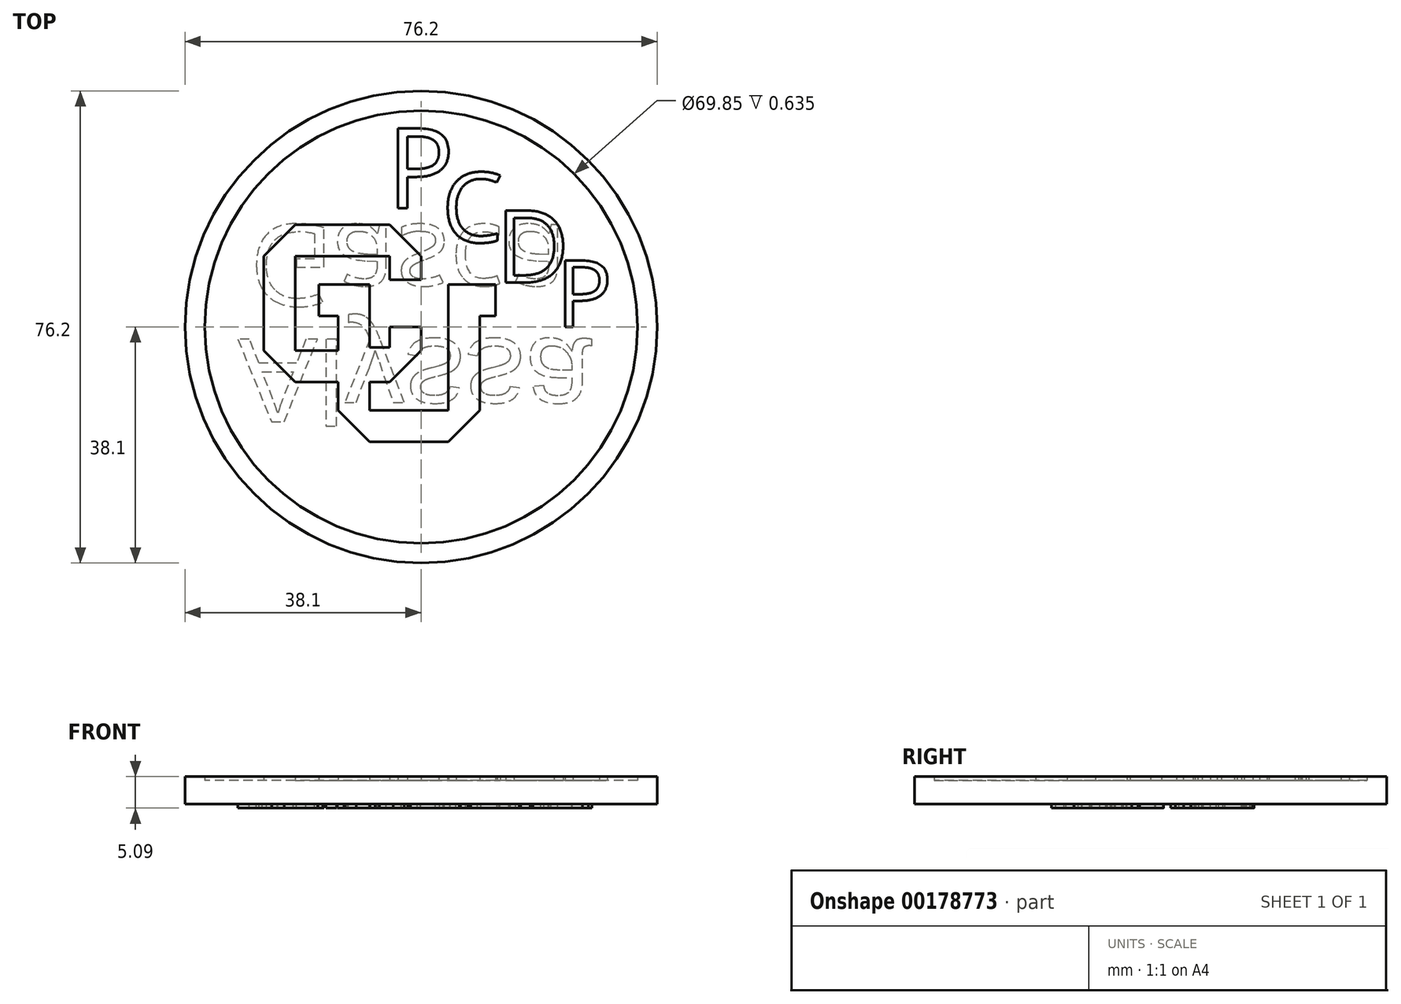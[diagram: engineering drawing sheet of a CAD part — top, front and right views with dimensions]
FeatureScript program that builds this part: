
annotation { "Feature Type Name" : "Feature", "Feature Type Description" : "" }
export const myFeature = defineFeature(function(context is Context, id is Id, definition is map)
    precondition{}
    {
        {
            var Q0;
            Q0=qCreatedBy(makeId("Top.planeOp"),FACE);
            var sketch = newSketch(context, id + "F0", { "sketchPlane" : qUnion([Q0])});
            skCircle(sketch, "E0", {"center": v(0, 0) * mm, "radius": 38.1 * mm});
            skSolve(sketch);
        }
        {
            var Q0;
            Q0=makeQuery(id+"F0.imprint","IMPRINT",FACE,{"disambiguationData":[TD([[makeQuery(id+"F0.imprint","IMPRINT",EDGE,{"derivedFrom":sQuery(id+"F0.wireOp",EDGE,"E0")}),1.0]])]});
            extrude(context, id + "F1", {"entities" : qUnion([Q0]), "depth" : 3.8 * mm});
        }
        {
            var Q0;
            Q0=makeQuery(id+"F1.opExtrude","CAP_FACE",FACE,{"disambiguationData":[OSD([sQuery(id+"F0.wireOp",EDGE,"E0")])],"isStart":false});
            var sketch = newSketch(context, id + "F2", { "sketchPlane" : qUnion([Q0])});
            skCircle(sketch, "E1", {"center": v(0, 0) * mm, "radius": 38.1 * mm});
            skCircle(sketch, "E2", {"center": v(0, 0) * mm, "radius": 34.93 * mm});
            skLineSegment(sketch, "E3", {"start": v(0, 0) * mm, "end": v(0, -3.81) * mm});
            skLineSegment(sketch, "E4", {"start": v(0, -3.81) * mm, "end": v(-5.08, -8.9) * mm});
            skLineSegment(sketch, "E5", {"start": v(-20.32, -8.9) * mm, "end": v(-25.4, -3.81) * mm});
            skLineSegment(sketch, "E6", {"start": v(-25.4, -3.81) * mm, "end": v(-25.4, 11.43) * mm});
            skLineSegment(sketch, "E7", {"start": v(-25.4, 11.43) * mm, "end": v(-20.32, 16.5) * mm});
            skLineSegment(sketch, "E8", {"start": v(-20.32, 16.5) * mm, "end": v(-5.08, 16.5) * mm});
            skLineSegment(sketch, "E9", {"start": v(-5.08, 16.5) * mm, "end": v(0, 11.43) * mm});
            skLineSegment(sketch, "E10", {"start": v(0, 11.43) * mm, "end": v(0, 7.62) * mm});
            skLineSegment(sketch, "E11", {"start": v(0, 7.62) * mm, "end": v(-5.08, 7.62) * mm});
            skLineSegment(sketch, "E12", {"start": v(-5.08, 7.62) * mm, "end": v(-5.08, 11.43) * mm});
            skLineSegment(sketch, "E13", {"start": v(-5.08, 11.43) * mm, "end": v(-20.32, 11.43) * mm});
            skLineSegment(sketch, "E14", {"start": v(-20.32, 11.43) * mm, "end": v(-20.32, -3.81) * mm});
            skLineSegment(sketch, "E15", {"start": v(-5.08, -3.28) * mm, "end": v(-5.08, 0) * mm});
            skLineSegment(sketch, "E16", {"start": v(-5.08, 0) * mm, "end": v(0, 0) * mm});
            skLineSegment(sketch, "E17", {"start": v(-16.51, 6.88) * mm, "end": v(-16.51, 1.8) * mm});
            skLineSegment(sketch, "E18", {"start": v(-16.51, 1.8) * mm, "end": v(-13.36, 1.8) * mm});
            skLineSegment(sketch, "E19", {"start": v(-16.51, 6.88) * mm, "end": v(-8.28, 6.88) * mm});
            skLineSegment(sketch, "E20", {"start": v(-13.36, -13.44) * mm, "end": v(-8.28, -18.52) * mm});
            skLineSegment(sketch, "E21", {"start": v(-8.28, -18.52) * mm, "end": v(4.42, -18.52) * mm});
            skLineSegment(sketch, "E22", {"start": v(4.42, -18.52) * mm, "end": v(9.5, -13.44) * mm});
            skLineSegment(sketch, "E23", {"start": v(9.5, -13.44) * mm, "end": v(9.5, 1.8) * mm});
            skLineSegment(sketch, "E24", {"start": v(9.5, 1.8) * mm, "end": v(12.04, 1.8) * mm});
            skLineSegment(sketch, "E25", {"start": v(12.04, 1.8) * mm, "end": v(12.04, 6.88) * mm});
            skLineSegment(sketch, "E26", {"start": v(12.04, 6.88) * mm, "end": v(4.42, 6.88) * mm});
            skLineSegment(sketch, "E27", {"start": v(4.42, 6.88) * mm, "end": v(4.42, -13.44) * mm});
            skLineSegment(sketch, "E28", {"start": v(-13.36, 1.8) * mm, "end": v(-13.36, -3.81) * mm});
            skLineSegment(sketch, "E29", {"start": v(-20.32, -3.81) * mm, "end": v(-13.36, -3.81) * mm});
            skLineSegment(sketch, "E30", {"start": v(-20.32, -8.9) * mm, "end": v(-13.36, -8.9) * mm});
            skLineSegment(sketch, "E31", {"start": v(-13.36, -8.9) * mm, "end": v(-13.36, -13.44) * mm});
            skLineSegment(sketch, "E32", {"start": v(-8.28, -3.28) * mm, "end": v(-5.08, -3.28) * mm});
            skLineSegment(sketch, "E33", {"start": v(-5.08, -8.9) * mm, "end": v(-8.28, -8.9) * mm});
            skLineSegment(sketch, "E34", {"start": v(4.42, -13.44) * mm, "end": v(-8.28, -13.44) * mm});
            skLineSegment(sketch, "E35", {"start": v(-8.28, -13.44) * mm, "end": v(-8.28, -8.9) * mm});
            skLineSegment(sketch, "E36", {"start": v(-8.28, 6.88) * mm, "end": v(-8.28, -3.28) * mm});
            skText(sketch, "E37", { "text": "P", "fontName": "OpenSans-Regular.ttf"});
            skText(sketch, "E38", { "text": "C", "fontName": "OpenSans-Regular.ttf"});
            skText(sketch, "E39", { "text": "D", "fontName": "OpenSans-Regular.ttf"});
            skText(sketch, "E40", { "text": "P", "fontName": "OpenSans-Regular.ttf"});
            const initialGuessF2  = {"E37": [-0.00552, 0.01914, 1, 0, 0.01302], "E38": [0.00333, 0.01368, 1, 0, 0.01132], "E39": [0.01205, 0.00717, 1, 0, 0.01171], "E40": [0.02181, 0, 1, 0, 0.0108]};
            skSetInitialGuess(sketch, initialGuessF2);
            skSolve(sketch);
        }
        {
            var Q0;
            Q0=makeQuery(id+"F2.imprint","IMPRINT",FACE,{"disambiguationData":[TD([[makeQuery(id+"F2.imprint","IMPRINT",EDGE,{"derivedFrom":sQuery(id+"F2.wireOp",EDGE,"E3")}),-1.0]])]});
            var Q1;
            Q1=makeQuery(id+"F2.imprint","IMPRINT",FACE,{"disambiguationData":[TD([[makeQuery(id+"F2.imprint","IMPRINT",EDGE,{"derivedFrom":sQuery(id+"F2.wireOp",EDGE,"E37.sketch_text.stroke-0")}),-1.0]])]});
            var Q2;
            Q2=makeQuery(id+"F2.imprint","IMPRINT",FACE,{"disambiguationData":[TD([[makeQuery(id+"F2.imprint","IMPRINT",EDGE,{"derivedFrom":sQuery(id+"F2.wireOp",EDGE,"E1")}),1.0]])]});
            var Q3;
            Q3=makeQuery(id+"F2.imprint","IMPRINT",FACE,{"disambiguationData":[TD([[makeQuery(id+"F2.imprint","IMPRINT",EDGE,{"derivedFrom":sQuery(id+"F2.wireOp",EDGE,"E38.sketch_text.stroke-0")}),-1.0]])]});
            var Q4;
            Q4=makeQuery(id+"F2.imprint","IMPRINT",FACE,{"disambiguationData":[TD([[makeQuery(id+"F2.imprint","IMPRINT",EDGE,{"derivedFrom":sQuery(id+"F2.wireOp",EDGE,"E39.sketch_text.stroke-0")}),-1.0]])]});
            var Q5;
            Q5=makeQuery(id+"F2.imprint","IMPRINT",FACE,{"disambiguationData":[TD([[makeQuery(id+"F2.imprint","IMPRINT",EDGE,{"derivedFrom":sQuery(id+"F2.wireOp",EDGE,"E40.sketch_text.stroke-0")}),-1.0]])]});
            extrude(context, id + "F3", {"entities" : qUnion([Q0, Q1, Q2, Q3, Q4, Q5]), "operationType" : NewBodyOperationType.ADD, "depth" : 0.64 * mm});
        }
        {
            var Q0;
            Q0=makeQuery(id+"F1.opExtrude","CAP_FACE",FACE,{"disambiguationData":[OSD([sQuery(id+"F0.wireOp",EDGE,"E0")])],"isStart":true});
            var sketch = newSketch(context, id + "F4", { "sketchPlane" : qUnion([Q0])});
            skText(sketch, "E41", { "text": "Alyssa", "fontName": "Arimo-Regular.ttf"});
            skText(sketch, "E42", { "text": "Gasca", "fontName": "OpenSans-Regular.ttf"});
            const initialGuessF4  = {"E41": [-0.02963, 0.00195, 1, 0, 0.01398], "E42": [-0.02769, -0.0165, 1, 0, 0.0132]};
            skSetInitialGuess(sketch, initialGuessF4);
            skSolve(sketch);
        }
        {
            var Q0;
            Q0 = qSketchRegion(id + "F4", true);
            extrude(context, id + "F5", {"entities" : qUnion([Q0]), "operationType" : NewBodyOperationType.ADD, "depth" : 0.64 * mm});
        }
    });
